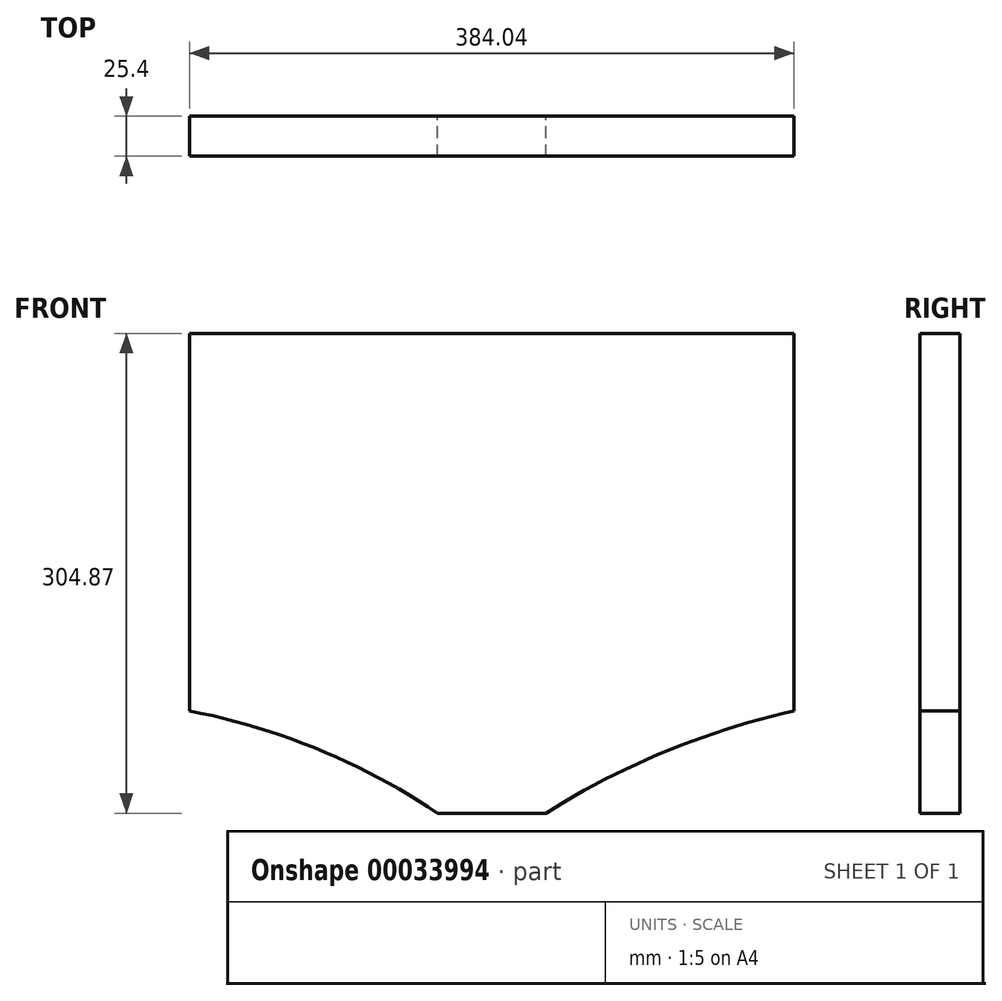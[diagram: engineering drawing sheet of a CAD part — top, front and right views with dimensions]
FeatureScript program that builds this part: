
annotation { "Feature Type Name" : "Feature", "Feature Type Description" : "" }
export const myFeature = defineFeature(function(context is Context, id is Id, definition is map)
    precondition{}
    {
        {
            var Q0;
            Q0=qCreatedBy(makeId("Front.planeOp"),FACE);
            var sketch = newSketch(context, id + "F0", { "sketchPlane" : qUnion([Q0])});
            skLineSegment(sketch, "E0.rect.top", {"start": v(-192.02, 119.95) * mm, "end": v(192.02, 119.95) * mm});
            skLineSegment(sketch, "E0.rect.left", {"start": v(-192.02, -119.95) * mm, "end": v(-192.02, 119.95) * mm});
            skLineSegment(sketch, "E0.rect.right", {"start": v(192.02, -119.95) * mm, "end": v(192.02, 119.95) * mm});
            skPoint(sketch, "E0.rect.middle", {"position": v(0, 0) * mm});
            skLineSegment(sketch, "E1", {"start": v(-34.52, -184.92) * mm, "end": v(34.52, -184.92) * mm});
            skFitSpline(sketch, "E2", {"points": [v(-192.02, -119.95) * mm, v(-34.52, -184.92) * mm], "startDerivative": vector(164.46, -30.44) * mm, "endDerivative": vector(134.08, -92.7) * mm});
            skFitSpline(sketch, "E3", {"points": [v(34.52, -184.92) * mm, v(192.02, -119.95) * mm], "startDerivative": vector(132.26, 85.88) * mm, "endDerivative": vector(164.9, 35.67) * mm});
            skSolve(sketch);
        }
        {
            var Q0;
            Q0=makeQuery(id+"F0.imprint","IMPRINT",FACE,{"disambiguationData":[TD([[makeQuery(id+"F0.imprint","IMPRINT",EDGE,{"derivedFrom":sQuery(id+"F0.wireOp",EDGE,"E0.rect.top")}),-1.0]])]});
            extrude(context, id + "F1", {"entities" : qUnion([Q0]), "depth" : 25.4 * mm});
        }
    });
